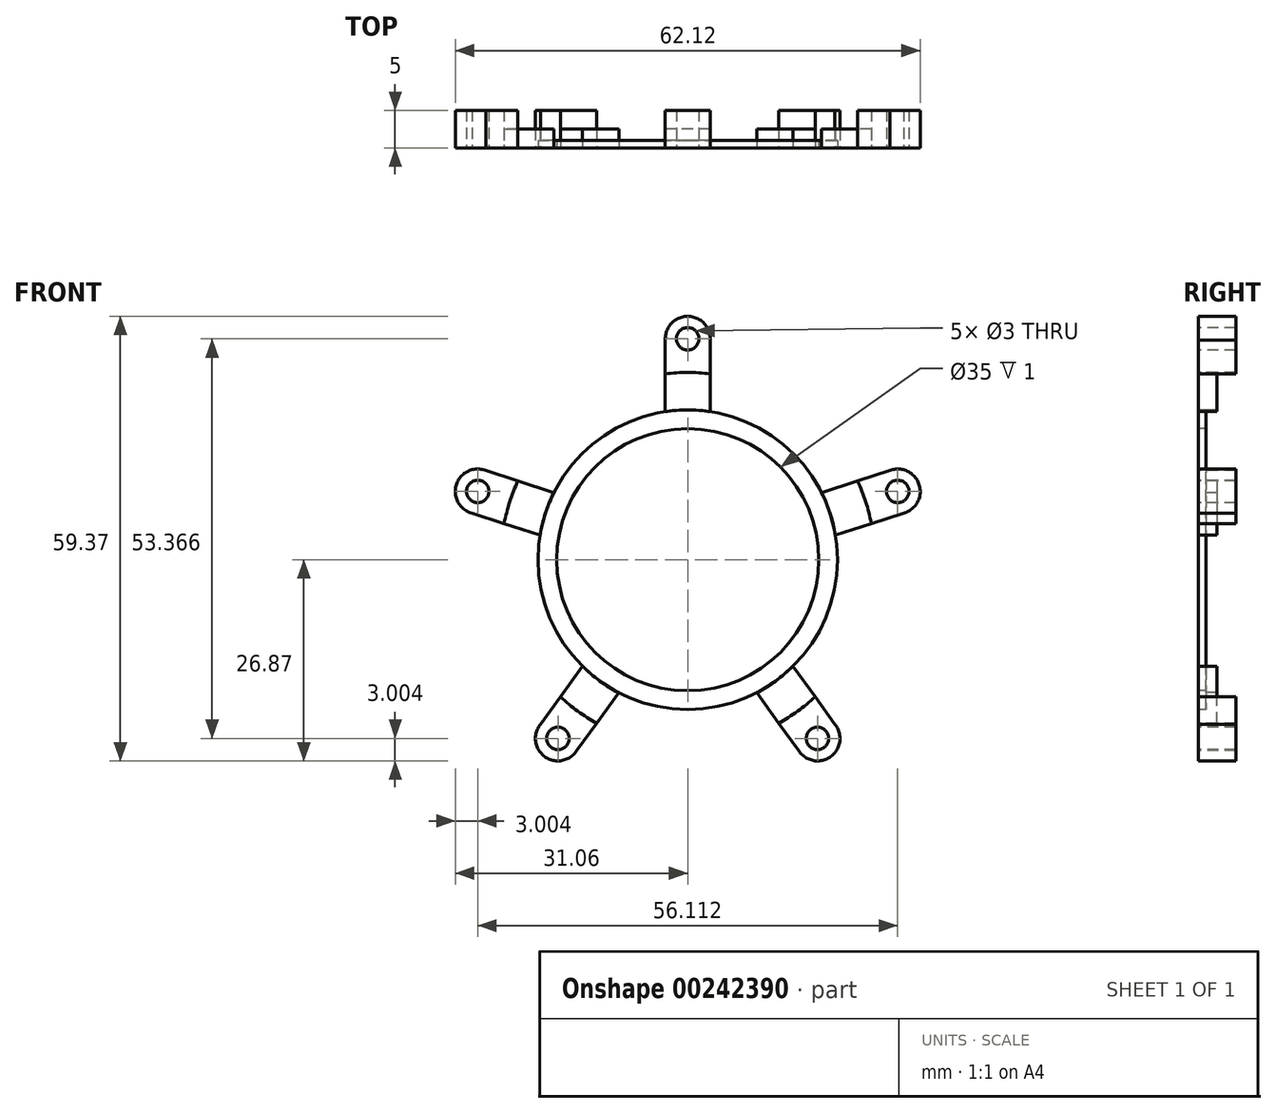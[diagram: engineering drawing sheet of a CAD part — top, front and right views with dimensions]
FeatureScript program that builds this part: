
annotation { "Feature Type Name" : "Feature", "Feature Type Description" : "" }
export const myFeature = defineFeature(function(context is Context, id is Id, definition is map)
    precondition{}
    {
        {
            var Q0;
            Q0=qCreatedBy(makeId("Front.planeOp"),FACE);
            var sketch = newSketch(context, id + "F0", { "sketchPlane" : qUnion([Q0])});
            skCircle(sketch, "E0", {"center": v(0, 0) * mm, "radius": 29.5 * mm, "construction": true});
            skCircle(sketch, "E1", {"center": v(0, 29.5) * mm, "radius": 1.5 * mm});
            skArc(sketch, "E2", {"start": v(3, 29.35) * mm, "mid": v(0, 32.5) * mm, "end": v(-3, 29.35) * mm});
            skCircle(sketch, "E3", {"center": v(0, 0) * mm, "radius": 20 * mm});
            skCircle(sketch, "E4", {"center": v(0, 0) * mm, "radius": 17.5 * mm});
            skLineSegment(sketch, "E5", {"start": v(-3, 29.35) * mm, "end": v(-3, 19.77) * mm});
            skLineSegment(sketch, "E6", {"start": v(3, 29.35) * mm, "end": v(3, 19.77) * mm});
            skCircle(sketch, "E7.1.0", {"center": v(-28.06, 9.12) * mm, "radius": 1.5 * mm});
            skLineSegment(sketch, "E7.1.1", {"start": v(-28.84, 6.22) * mm, "end": v(-19.73, 3.26) * mm});
            skLineSegment(sketch, "E7.1.2", {"start": v(-26.99, 11.92) * mm, "end": v(-17.88, 8.96) * mm});
            skArc(sketch, "E7.1.3", {"start": v(-26.99, 11.92) * mm, "mid": v(-30.9, 10.04) * mm, "end": v(-28.84, 6.22) * mm});
            skCircle(sketch, "E7.2.0", {"center": v(-17.34, -23.87) * mm, "radius": 1.5 * mm});
            skLineSegment(sketch, "E7.2.1", {"start": v(-14.83, -25.5) * mm, "end": v(-9.2, -17.76) * mm});
            skLineSegment(sketch, "E7.2.2", {"start": v(-19.67, -21.98) * mm, "end": v(-14.05, -14.24) * mm});
            skArc(sketch, "E7.2.3", {"start": v(-19.67, -21.98) * mm, "mid": v(-19.1, -26.3) * mm, "end": v(-14.83, -25.5) * mm});
            skCircle(sketch, "E7.3.0", {"center": v(17.34, -23.87) * mm, "radius": 1.5 * mm});
            skLineSegment(sketch, "E7.3.1", {"start": v(19.67, -21.98) * mm, "end": v(14.05, -14.24) * mm});
            skLineSegment(sketch, "E7.3.2", {"start": v(14.83, -25.5) * mm, "end": v(9.2, -17.76) * mm});
            skArc(sketch, "E7.3.3", {"start": v(14.83, -25.5) * mm, "mid": v(19.1, -26.3) * mm, "end": v(19.67, -21.98) * mm});
            skCircle(sketch, "E7.4.0", {"center": v(28.06, 9.12) * mm, "radius": 1.5 * mm});
            skLineSegment(sketch, "E7.4.1", {"start": v(26.99, 11.92) * mm, "end": v(17.88, 8.96) * mm});
            skLineSegment(sketch, "E7.4.2", {"start": v(28.84, 6.22) * mm, "end": v(19.73, 3.26) * mm});
            skArc(sketch, "E7.4.3", {"start": v(28.84, 6.22) * mm, "mid": v(30.9, 10.04) * mm, "end": v(26.99, 11.92) * mm});
            skCircle(sketch, "E8", {"center": v(0, 0) * mm, "radius": 25 * mm});
            skCircle(sketch, "E9", {"center": v(0, 0) * mm, "radius": 32.5 * mm});
            skSolve(sketch);
        }
        {
            var Q0;
            Q0=makeQuery(id+"F0.imprint","IMPRINT",FACE,{"disambiguationData":[TD([[makeQuery(id+"F0.imprint","IMPRINT",EDGE,{"derivedFrom":sQuery(id+"F0.wireOp",EDGE,"E7.1.0")}),-1.0]])]});
            var Q1;
            Q1=makeQuery(id+"F0.imprint","IMPRINT",FACE,{"disambiguationData":[TD([[makeQuery(id+"F0.imprint","IMPRINT",EDGE,{"derivedFrom":sQuery(id+"F0.wireOp",EDGE,"E1")}),-1.0]])]});
            var Q2;
            Q2=makeQuery(id+"F0.imprint","IMPRINT",FACE,{"disambiguationData":[TD([[makeQuery(id+"F0.imprint","IMPRINT",EDGE,{"derivedFrom":sQuery(id+"F0.wireOp",EDGE,"E7.4.0")}),-1.0]])]});
            var Q3;
            Q3=makeQuery(id+"F0.imprint","IMPRINT",FACE,{"disambiguationData":[TD([[makeQuery(id+"F0.imprint","IMPRINT",EDGE,{"derivedFrom":sQuery(id+"F0.wireOp",EDGE,"E7.3.0")}),-1.0]])]});
            var Q4;
            Q4=makeQuery(id+"F0.imprint","IMPRINT",FACE,{"disambiguationData":[TD([[makeQuery(id+"F0.imprint","IMPRINT",EDGE,{"derivedFrom":sQuery(id+"F0.wireOp",EDGE,"E7.2.0")}),-1.0]])]});
            extrude(context, id + "F1", {"entities" : qUnion([Q0, Q1, Q2, Q3, Q4]), "oppositeDirection" : true, "depth" : 5 * mm});
        }
        {
            var Q0;
            Q0=makeQuery(id+"F0.imprint","IMPRINT",FACE,{"disambiguationData":[TD([[makeQuery(id+"F0.imprint","IMPRINT",EDGE,{"derivedFrom":sQuery(id+"F0.wireOp",EDGE,"E4")}),-1.0]])]});
            extrude(context, id + "F2", {"entities" : qUnion([Q0]), "oppositeDirection" : true, "depth" : 1 * mm});
        }
        {
            var Q0;
            {var subQ0=sQuery(id+"F0.wireOp",EDGE,"E7.2.1");var subQ1=sQuery(id+"F0.wireOp",EDGE,"E3");var subQ2=makeQuery(id+"F0.imprint","INTERSECT",VERTEX,{"derivedFrom":[subQ1,subQ0]});Q0=makeQuery(id+"F0.imprint","IMPRINT",FACE,{"disambiguationData":[TD([[makeQuery(id+"F0.imprint","IMPRINT",EDGE,{"disambiguationData":[TD([[subQ2,1.0]])],"derivedFrom":subQ1}),-1.0]])]});}
            var Q1;
            {var subQ0=sQuery(id+"F0.wireOp",EDGE,"E7.1.1");var subQ1=sQuery(id+"F0.wireOp",EDGE,"E3");var subQ2=makeQuery(id+"F0.imprint","INTERSECT",VERTEX,{"derivedFrom":[subQ1,subQ0]});Q1=makeQuery(id+"F0.imprint","IMPRINT",FACE,{"disambiguationData":[TD([[makeQuery(id+"F0.imprint","IMPRINT",EDGE,{"disambiguationData":[TD([[subQ2,1.0]])],"derivedFrom":subQ1}),-1.0]])]});}
            var Q2;
            {var subQ0=sQuery(id+"F0.wireOp",EDGE,"E5");var subQ1=sQuery(id+"F0.wireOp",EDGE,"E3");var subQ2=makeQuery(id+"F0.imprint","INTERSECT",VERTEX,{"derivedFrom":[subQ1,subQ0]});Q2=makeQuery(id+"F0.imprint","IMPRINT",FACE,{"disambiguationData":[TD([[makeQuery(id+"F0.imprint","IMPRINT",EDGE,{"disambiguationData":[TD([[subQ2,1.0]])],"derivedFrom":subQ1}),-1.0]])]});}
            var Q3;
            {var subQ0=sQuery(id+"F0.wireOp",EDGE,"E7.4.1");var subQ1=sQuery(id+"F0.wireOp",EDGE,"E3");var subQ2=makeQuery(id+"F0.imprint","INTERSECT",VERTEX,{"derivedFrom":[subQ1,subQ0]});Q3=makeQuery(id+"F0.imprint","IMPRINT",FACE,{"disambiguationData":[TD([[makeQuery(id+"F0.imprint","IMPRINT",EDGE,{"disambiguationData":[TD([[subQ2,1.0]])],"derivedFrom":subQ1}),-1.0]])]});}
            var Q4;
            {var subQ0=sQuery(id+"F0.wireOp",EDGE,"E7.3.1");var subQ1=sQuery(id+"F0.wireOp",EDGE,"E3");var subQ2=makeQuery(id+"F0.imprint","INTERSECT",VERTEX,{"derivedFrom":[subQ1,subQ0]});Q4=makeQuery(id+"F0.imprint","IMPRINT",FACE,{"disambiguationData":[TD([[makeQuery(id+"F0.imprint","IMPRINT",EDGE,{"disambiguationData":[TD([[subQ2,1.0]])],"derivedFrom":subQ1}),-1.0]])]});}
            extrude(context, id + "F3", {"entities" : qUnion([Q0, Q1, Q2, Q3, Q4]), "oppositeDirection" : true, "depth" : 2.5 * mm});
        }
    });
